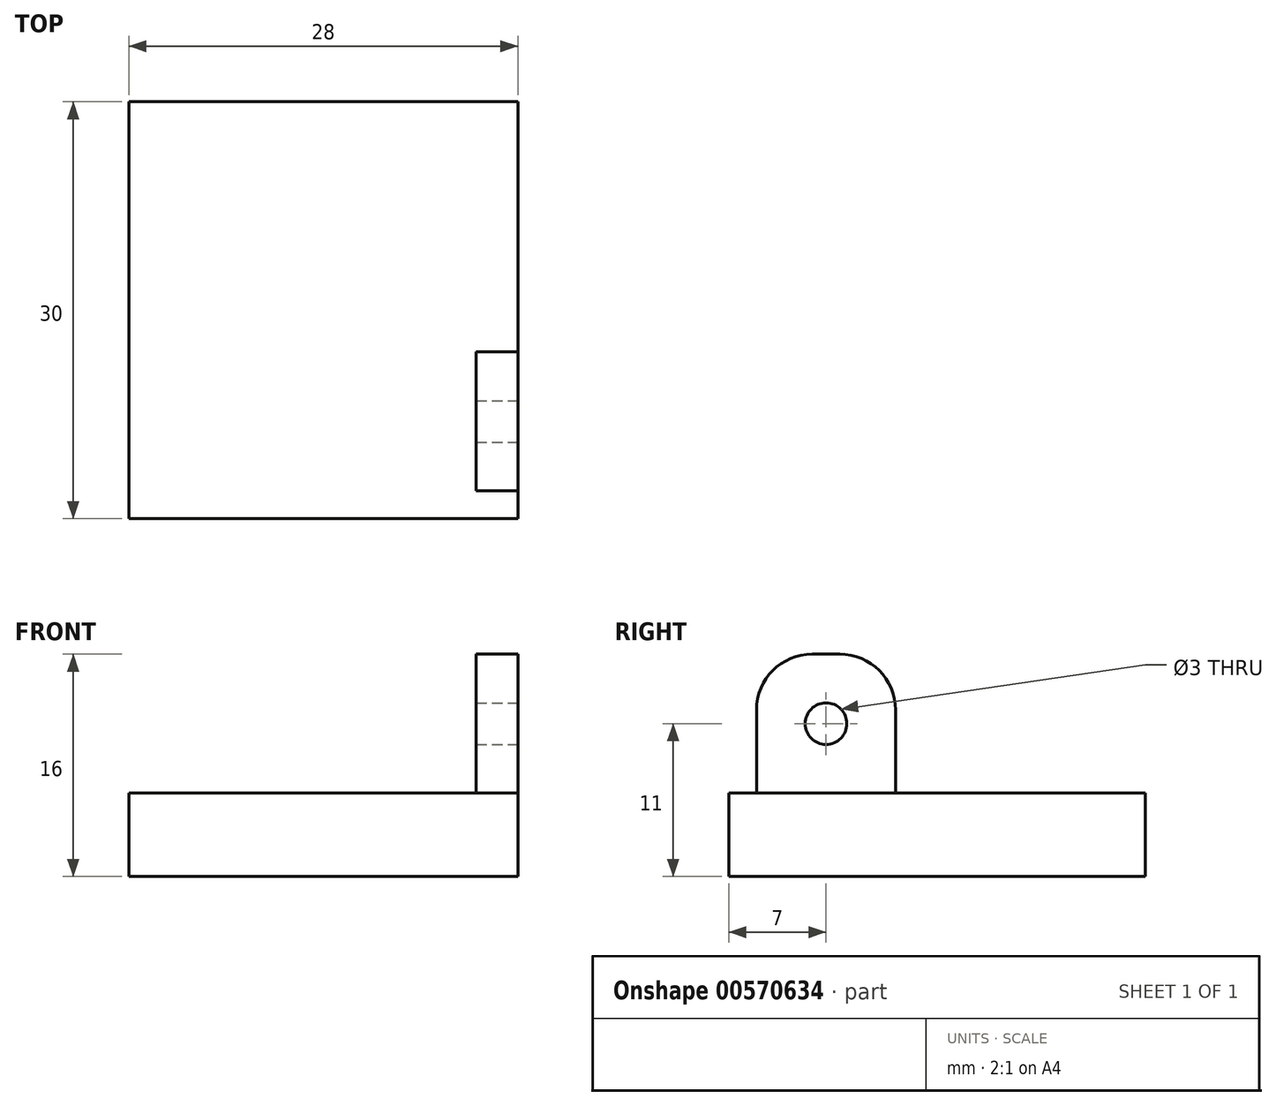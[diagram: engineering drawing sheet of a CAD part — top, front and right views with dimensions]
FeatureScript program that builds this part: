
annotation { "Feature Type Name" : "Feature", "Feature Type Description" : "" }
export const myFeature = defineFeature(function(context is Context, id is Id, definition is map)
    precondition{}
    {
        {
            var Q0;
            Q0=qCreatedBy(makeId("Top.planeOp"),FACE);
            var sketch = newSketch(context, id + "F0", { "sketchPlane" : qUnion([Q0])});
            skLineSegment(sketch, "E0.bottom", {"start": v(0, 0) * mm, "end": v(28, 0) * mm});
            skLineSegment(sketch, "E0.top", {"start": v(0, 30) * mm, "end": v(28, 30) * mm});
            skLineSegment(sketch, "E0.left", {"start": v(0, 0) * mm, "end": v(0, 30) * mm});
            skLineSegment(sketch, "E0.right", {"start": v(28, 0) * mm, "end": v(28, 30) * mm});
            skSolve(sketch);
        }
        {
            var Q0;
            Q0 = qSketchRegion(id + "F0", true);
            extrude(context, id + "F1", {"entities" : qUnion([Q0]), "depth" : 6 * mm, "offsetDistance" : 25 * mm});
        }
        {
            var Q0;
            Q0=makeQuery(id+"F1.opExtrude","SWEPT_FACE",FACE,{"disambiguationData":[OSD([sQuery(id+"F0.wireOp",EDGE,"E0.right")])]});
            var sketch = newSketch(context, id + "F2", { "sketchPlane" : qUnion([Q0])});
            skLineSegment(sketch, "E1.bottom", {"start": v(2, 6) * mm, "end": v(12, 6) * mm});
            skLineSegment(sketch, "E1.top", {"start": v(6, 16) * mm, "end": v(8, 16) * mm});
            skLineSegment(sketch, "E1.left", {"start": v(2, 6) * mm, "end": v(2, 12) * mm});
            skLineSegment(sketch, "E1.right", {"start": v(12, 6) * mm, "end": v(12, 12) * mm});
            skPoint(sketch, "E2.visualSharp", {"position": v(2, 16) * mm});
            skArc(sketch, "E2.filletArc", {"start": v(6, 16) * mm, "mid": v(3.17, 14.83) * mm, "end": v(2, 12) * mm});
            skPoint(sketch, "E3.visualSharp", {"position": v(12, 16) * mm});
            skArc(sketch, "E3.filletArc", {"start": v(12, 12) * mm, "mid": v(10.83, 14.83) * mm, "end": v(8, 16) * mm});
            skCircle(sketch, "E4", {"center": v(7, 11) * mm, "radius": 1.5 * mm});
            skPoint(sketch, "E4.centerSnap0", {"position": v(7, 6) * mm});
            skSolve(sketch);
        }
        {
            var Q0;
            Q0=makeQuery(id+"F2.imprint","IMPRINT",FACE,{"disambiguationData":[TD([[makeQuery(id+"F2.imprint","IMPRINT",EDGE,{"derivedFrom":sQuery(id+"F2.wireOp",EDGE,"E1.bottom")}),1.0]])]});
            extrude(context, id + "F3", {"entities" : qUnion([Q0]), "oppositeDirection" : true, "depth" : 3 * mm, "offsetDistance" : 25 * mm});
        }
    });
